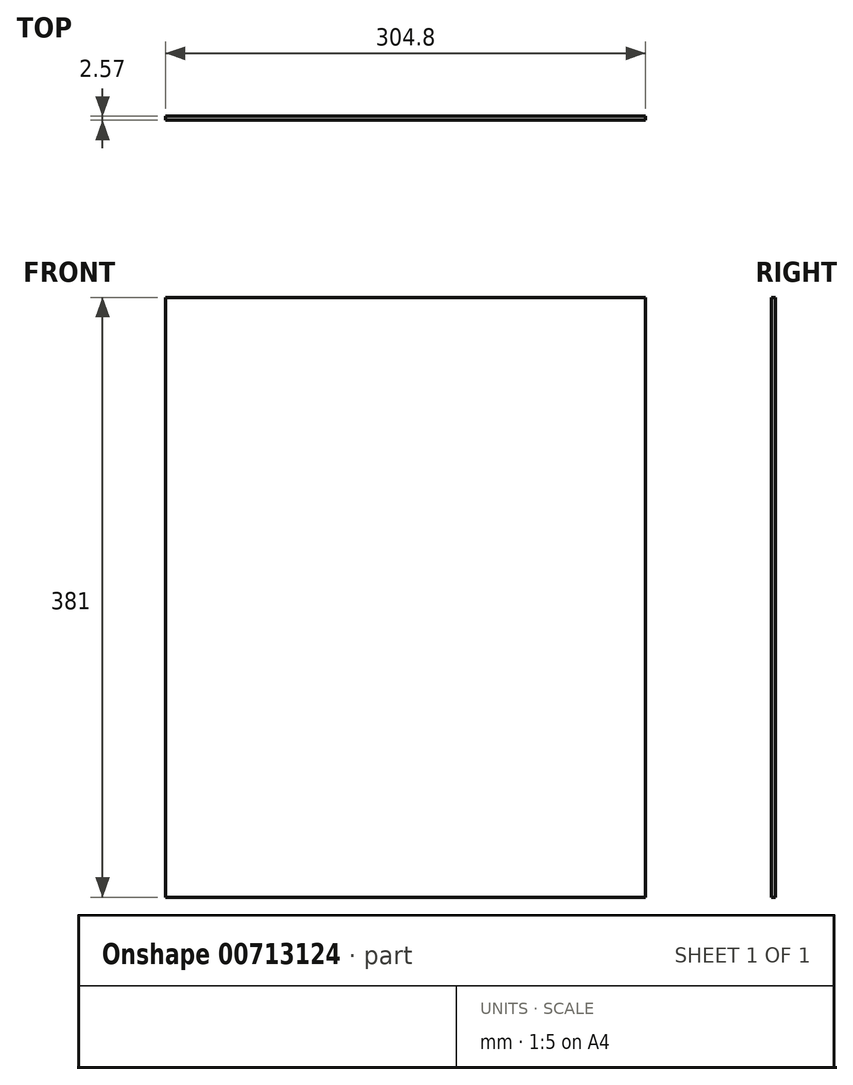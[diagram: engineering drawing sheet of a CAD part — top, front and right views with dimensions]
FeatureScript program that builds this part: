
annotation { "Feature Type Name" : "Feature", "Feature Type Description" : "" }
export const myFeature = defineFeature(function(context is Context, id is Id, definition is map)
    precondition{}
    {
        {
            var Q0;
            Q0=qCreatedBy(makeId("Front.planeOp"),FACE);
            var sketch = newSketch(context, id + "F0", { "sketchPlane" : qUnion([Q0])});
            skLineSegment(sketch, "E0.bottom", {"start": v(-152.4, 190.5) * mm, "end": v(152.4, 190.5) * mm});
            skLineSegment(sketch, "E0.top", {"start": v(-152.4, -190.5) * mm, "end": v(152.4, -190.5) * mm});
            skLineSegment(sketch, "E0.left", {"start": v(-152.4, 190.5) * mm, "end": v(-152.4, -190.5) * mm});
            skLineSegment(sketch, "E0.right", {"start": v(152.4, 190.5) * mm, "end": v(152.4, -190.5) * mm});
            skPoint(sketch, "E0.middle", {"position": v(0, 0) * mm});
            skSolve(sketch);
        }
        {
            var Q0;
            Q0=makeQuery(id+"F0.imprint","IMPRINT",FACE,{"disambiguationData":[TD([[makeQuery(id+"F0.imprint","IMPRINT",EDGE,{"derivedFrom":sQuery(id+"F0.wireOp",EDGE,"E0.bottom")}),-1.0]])]});
            extrude(context, id + "F1", {"entities" : qUnion([Q0]), "depth" : 2.54 * mm, "offsetDistance" : 25.4 * mm});
        }
        {
            var Q0;
            Q0=makeQuery(id+"F0.imprint","IMPRINT",FACE,{"disambiguationData":[TD([[makeQuery(id+"F0.imprint","IMPRINT",EDGE,{"derivedFrom":sQuery(id+"F0.wireOp",EDGE,"E0.bottom")}),-1.0]])]});
            extrude(context, id + "F2", {"entities" : qUnion([Q0]), "operationType" : NewBodyOperationType.ADD, "oppositeDirection" : true, "depth" : 0.03 * mm, "offsetDistance" : 25.4 * mm});
        }
    });
